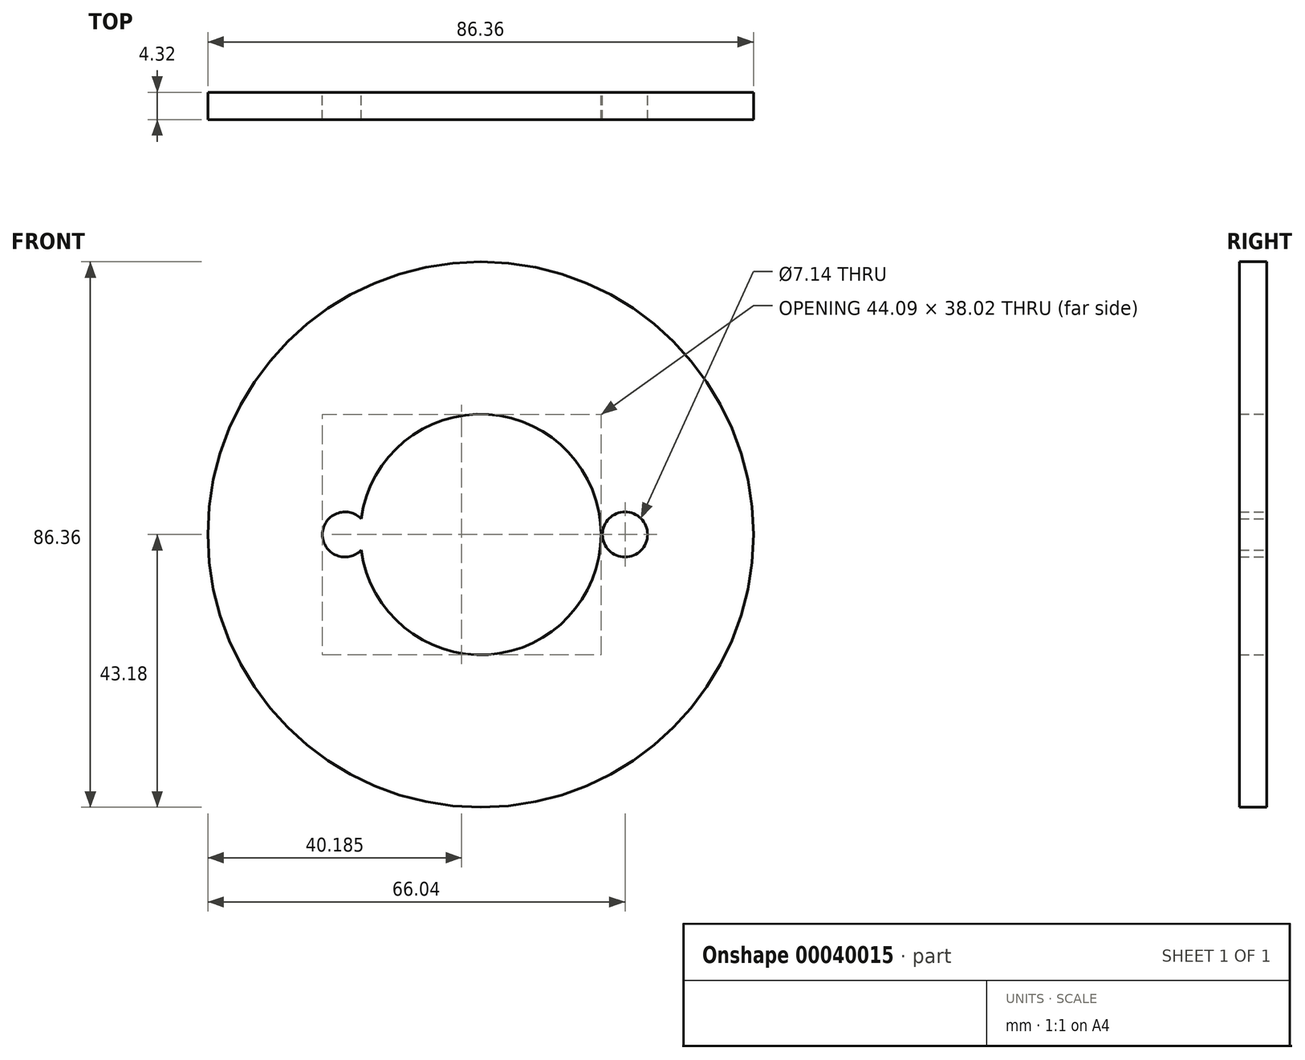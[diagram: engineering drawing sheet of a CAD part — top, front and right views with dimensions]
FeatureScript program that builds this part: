
annotation { "Feature Type Name" : "Feature", "Feature Type Description" : "" }
export const myFeature = defineFeature(function(context is Context, id is Id, definition is map)
    precondition{}
    {
        {
            var Q0;
            Q0=qCreatedBy(makeId("Front.planeOp"),FACE);
            var sketch = newSketch(context, id + "F0", { "sketchPlane" : qUnion([Q0])});
            skCircle(sketch, "E0", {"center": v(0, 0) * mm, "radius": 43.18 * mm});
            skCircle(sketch, "E1", {"center": v(0, 0) * mm, "radius": 6.35 * mm});
            skCircle(sketch, "E2", {"center": v(22.86, 0) * mm, "radius": 3.57 * mm});
            skCircle(sketch, "E3", {"center": v(-21.47, 0) * mm, "radius": 3.57 * mm});
            skCircle(sketch, "E4", {"center": v(0, 0) * mm, "radius": 19.05 * mm});
            skSolve(sketch);
        }
        {
            var Q0;
            Q0=makeQuery(id+"F0.imprint","IMPRINT",FACE,{"disambiguationData":[TD([[makeQuery(id+"F0.imprint","IMPRINT",EDGE,{"derivedFrom":sQuery(id+"F0.wireOp",EDGE,"E0")}),1.0]])]});
            extrude(context, id + "F1", {"entities" : qUnion([Q0]), "depth" : 4.32 * mm});
        }
    });
